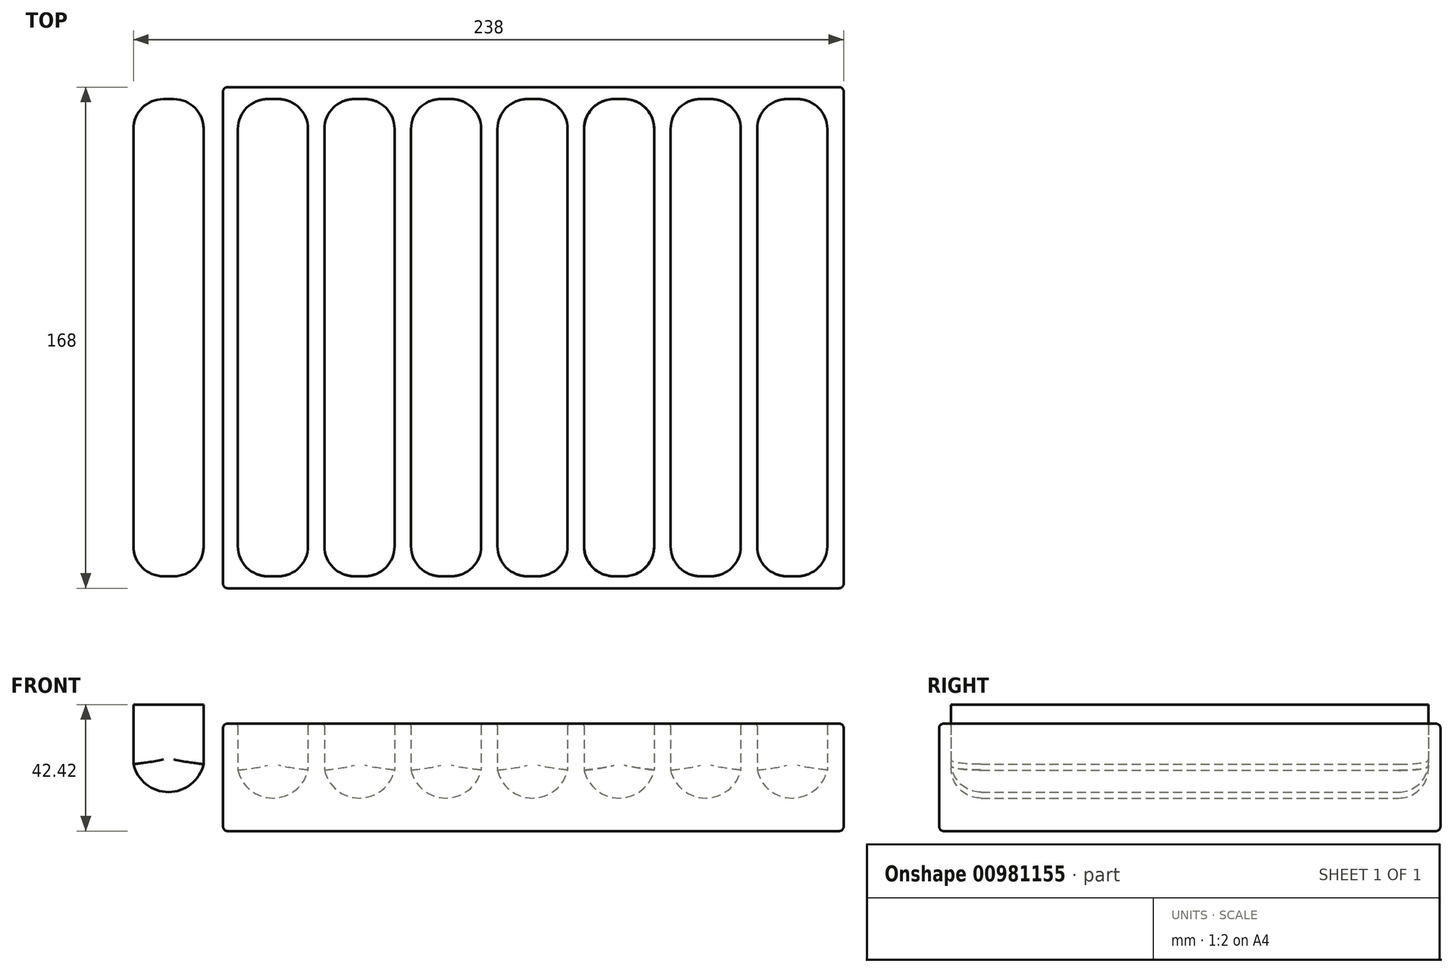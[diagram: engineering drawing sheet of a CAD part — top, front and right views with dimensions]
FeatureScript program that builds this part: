
annotation { "Feature Type Name" : "Feature", "Feature Type Description" : "" }
export const myFeature = defineFeature(function(context is Context, id is Id, definition is map)
    precondition{}
    {
        {
            var Q0;
            Q0=qCreatedBy(makeId("Top.planeOp"),FACE);
            var sketch = newSketch(context, id + "F0", { "sketchPlane" : qUnion([Q0])});
            skLineSegment(sketch, "E0.bottom", {"start": v(104, -84) * mm, "end": v(-104, -84) * mm});
            skLineSegment(sketch, "E0.top", {"start": v(104, 84) * mm, "end": v(-104, 84) * mm});
            skLineSegment(sketch, "E0.left", {"start": v(104, -84) * mm, "end": v(104, 84) * mm});
            skLineSegment(sketch, "E0.right", {"start": v(-104, -84) * mm, "end": v(-104, 84) * mm});
            skPoint(sketch, "E0.middle", {"position": v(0, 0) * mm});
            skSolve(sketch);
        }
        {
            var Q0;
            Q0=qSketchRegion(id+"F0",true);
            extrude(context, id + "F1", {"entities" : qUnion([Q0]), "depth" : 36 * mm, "offsetDistance" : 25 * mm});
        }
        {
            var Q0;
            Q0=qCreatedBy(makeId("Front.planeOp"),FACE);
            var sketch = newSketch(context, id + "F2", { "sketchPlane" : qUnion([Q0])});
            skLineSegment(sketch, "E1.bottom", {"start": v(-134, 42.42) * mm, "end": v(-110.5, 42.42) * mm});
            skLineSegment(sketch, "E1.top", {"start": v(-134, 22.42) * mm, "end": v(-110.5, 22.42) * mm});
            skLineSegment(sketch, "E1.left", {"start": v(-134, 42.42) * mm, "end": v(-134, 22.42) * mm});
            skLineSegment(sketch, "E1.right", {"start": v(-110.5, 42.42) * mm, "end": v(-110.5, 22.42) * mm});
            skArc(sketch, "E2", {"start": v(-134, 22.42) * mm, "mid": v(-122.25, 13.06) * mm, "end": v(-110.5, 22.42) * mm});
            skSolve(sketch);
        }
        {
            var Q0;
            Q0=makeQuery(id+"F2.imprint","IMPRINT",FACE,{"disambiguationData":[TD([[makeQuery(id+"F2.imprint","IMPRINT",EDGE,{"derivedFrom":sQuery(id+"F2.wireOp",EDGE,"E1.bottom")}),-1.0]])]});
            var Q1;
            Q1=makeQuery(id+"F2.imprint","IMPRINT",FACE,{"disambiguationData":[TD([[makeQuery(id+"F2.imprint","IMPRINT",EDGE,{"derivedFrom":sQuery(id+"F2.wireOp",EDGE,"E1.top")}),-1.0]])]});
            extrude(context, id + "F3", {"entities" : qUnion([Q0, Q1]), "depth" : 160 * mm, "offsetDistance" : 25 * mm, "symmetric" : true});
        }
        {
            var Q0;
            Q0=makeQuery(id+"F3.opExtrude","CAP_EDGE",EDGE,{"disambiguationData":[OSD([sQuery(id+"F2.wireOp",EDGE,"E1.left")])],"isStart":false});
            var Q1;
            Q1=makeQuery(id+"F3.opExtrude","CAP_EDGE",EDGE,{"disambiguationData":[OSD([sQuery(id+"F2.wireOp",EDGE,"E1.left")])],"isStart":true});
            var Q2;
            Q2=makeQuery(id+"F3.opExtrude","CAP_EDGE",EDGE,{"disambiguationData":[OSD([sQuery(id+"F2.wireOp",EDGE,"E1.right")])],"isStart":false});
            var Q3;
            Q3=makeQuery(id+"F3.opExtrude","CAP_EDGE",EDGE,{"disambiguationData":[OSD([sQuery(id+"F2.wireOp",EDGE,"E1.right")])],"isStart":true});
            var Q4;
            Q4=makeQuery(id+"F3.opExtrude","CAP_EDGE",EDGE,{"disambiguationData":[OSD([sQuery(id+"F2.wireOp",EDGE,"E2")])],"isStart":false});
            var Q5;
            Q5=makeQuery(id+"F3.opExtrude","CAP_EDGE",EDGE,{"disambiguationData":[OSD([sQuery(id+"F2.wireOp",EDGE,"E2")])],"isStart":true});
            fillet(context, id + "F4", {"entities" : qUnion([Q0, Q1, Q2, Q3, Q4, Q5]), "tangentPropagation" : true, "radius" : 10 * mm, "defaultsChanged" : true, "vertexSettings" : [], "allowEdgeOverflow" : false});
        }
        {
            var Q0;
            Q0=makeQuery(id+"F3.opExtrude","SWEPT_BODY",BODY,{"disambiguationData":[OSD([sQuery(id+"F2.wireOp",EDGE,"E1.bottom"),sQuery(id+"F2.wireOp",EDGE,"E1.left"),sQuery(id+"F2.wireOp",EDGE,"E1.right"),sQuery(id+"F2.wireOp",EDGE,"E2")])]});
            transform(context, id + "F5", {"entities" : qUnion([Q0]), "transformType" : TransformType.TRANSLATION_3D, "dx" : 35 * mm, "dy" : 0 * mm, "dz" : -2 * mm, "makeCopy" : true});
        }
        {
            var Q0;
            Q0=makeQuery(id+"F5.opPattern","COPY",BODY,{"derivedFrom":makeQuery(id+"F3.opExtrude","SWEPT_BODY",BODY,{"disambiguationData":[OSD([sQuery(id+"F2.wireOp",EDGE,"E1.bottom"),sQuery(id+"F2.wireOp",EDGE,"E1.left"),sQuery(id+"F2.wireOp",EDGE,"E1.right"),sQuery(id+"F2.wireOp",EDGE,"E2")])]}),"instanceName":"1"});
            transform(context, id + "F6", {"entities" : qUnion([Q0]), "transformType" : TransformType.TRANSLATION_3D, "dx" : 29 * mm, "dy" : 0 * mm, "dz" : 0 * mm, "makeCopy" : true});
        }
        {
            var Q0;
            Q0=makeQuery(id+"F6.opPattern","COPY",BODY,{"derivedFrom":makeQuery(id+"F5.opPattern","COPY",BODY,{"derivedFrom":makeQuery(id+"F3.opExtrude","SWEPT_BODY",BODY,{"disambiguationData":[OSD([sQuery(id+"F2.wireOp",EDGE,"E1.bottom"),sQuery(id+"F2.wireOp",EDGE,"E1.left"),sQuery(id+"F2.wireOp",EDGE,"E1.right"),sQuery(id+"F2.wireOp",EDGE,"E2")])]}),"instanceName":"1"}),"instanceName":"1"});
            transform(context, id + "F7", {"entities" : qUnion([Q0]), "transformType" : TransformType.TRANSLATION_3D, "dx" : 29 * mm, "dy" : 0 * mm, "dz" : 0 * mm, "makeCopy" : true});
        }
        {
            var Q0;
            Q0=makeQuery(id+"F7.opPattern","COPY",BODY,{"derivedFrom":makeQuery(id+"F6.opPattern","COPY",BODY,{"derivedFrom":makeQuery(id+"F5.opPattern","COPY",BODY,{"derivedFrom":makeQuery(id+"F3.opExtrude","SWEPT_BODY",BODY,{"disambiguationData":[OSD([sQuery(id+"F2.wireOp",EDGE,"E1.bottom"),sQuery(id+"F2.wireOp",EDGE,"E1.left"),sQuery(id+"F2.wireOp",EDGE,"E1.right"),sQuery(id+"F2.wireOp",EDGE,"E2")])]}),"instanceName":"1"}),"instanceName":"1"}),"instanceName":"1"});
            transform(context, id + "F8", {"entities" : qUnion([Q0]), "transformType" : TransformType.TRANSLATION_3D, "dx" : 29 * mm, "dy" : 0 * mm, "dz" : 0 * mm, "makeCopy" : true});
        }
        {
            var Q0;
            Q0=makeQuery(id+"F8.opPattern","COPY",BODY,{"derivedFrom":makeQuery(id+"F7.opPattern","COPY",BODY,{"derivedFrom":makeQuery(id+"F6.opPattern","COPY",BODY,{"derivedFrom":makeQuery(id+"F5.opPattern","COPY",BODY,{"derivedFrom":makeQuery(id+"F3.opExtrude","SWEPT_BODY",BODY,{"disambiguationData":[OSD([sQuery(id+"F2.wireOp",EDGE,"E1.bottom"),sQuery(id+"F2.wireOp",EDGE,"E1.left"),sQuery(id+"F2.wireOp",EDGE,"E1.right"),sQuery(id+"F2.wireOp",EDGE,"E2")])]}),"instanceName":"1"}),"instanceName":"1"}),"instanceName":"1"}),"instanceName":"1"});
            transform(context, id + "F9", {"entities" : qUnion([Q0]), "transformType" : TransformType.TRANSLATION_3D, "dx" : 29 * mm, "dy" : 0 * mm, "dz" : 0 * mm, "makeCopy" : true});
        }
        {
            var Q0;
            Q0=makeQuery(id+"F9.opPattern","COPY",BODY,{"derivedFrom":makeQuery(id+"F8.opPattern","COPY",BODY,{"derivedFrom":makeQuery(id+"F7.opPattern","COPY",BODY,{"derivedFrom":makeQuery(id+"F6.opPattern","COPY",BODY,{"derivedFrom":makeQuery(id+"F5.opPattern","COPY",BODY,{"derivedFrom":makeQuery(id+"F3.opExtrude","SWEPT_BODY",BODY,{"disambiguationData":[OSD([sQuery(id+"F2.wireOp",EDGE,"E1.bottom"),sQuery(id+"F2.wireOp",EDGE,"E1.left"),sQuery(id+"F2.wireOp",EDGE,"E1.right"),sQuery(id+"F2.wireOp",EDGE,"E2")])]}),"instanceName":"1"}),"instanceName":"1"}),"instanceName":"1"}),"instanceName":"1"}),"instanceName":"1"});
            transform(context, id + "F10", {"entities" : qUnion([Q0]), "transformType" : TransformType.TRANSLATION_3D, "dx" : 29 * mm, "dy" : 0 * mm, "dz" : 0 * mm, "makeCopy" : true});
        }
        {
            var Q0;
            Q0=makeQuery(id+"F10.opPattern","COPY",BODY,{"derivedFrom":makeQuery(id+"F9.opPattern","COPY",BODY,{"derivedFrom":makeQuery(id+"F8.opPattern","COPY",BODY,{"derivedFrom":makeQuery(id+"F7.opPattern","COPY",BODY,{"derivedFrom":makeQuery(id+"F6.opPattern","COPY",BODY,{"derivedFrom":makeQuery(id+"F5.opPattern","COPY",BODY,{"derivedFrom":makeQuery(id+"F3.opExtrude","SWEPT_BODY",BODY,{"disambiguationData":[OSD([sQuery(id+"F2.wireOp",EDGE,"E1.bottom"),sQuery(id+"F2.wireOp",EDGE,"E1.left"),sQuery(id+"F2.wireOp",EDGE,"E1.right"),sQuery(id+"F2.wireOp",EDGE,"E2")])]}),"instanceName":"1"}),"instanceName":"1"}),"instanceName":"1"}),"instanceName":"1"}),"instanceName":"1"}),"instanceName":"1"});
            transform(context, id + "F11", {"entities" : qUnion([Q0]), "transformType" : TransformType.TRANSLATION_3D, "dx" : 29 * mm, "dy" : 0 * mm, "dz" : 0 * mm, "makeCopy" : true});
        }
        {
            var Q0;
            Q0=makeQuery(id+"F5.opPattern","COPY",BODY,{"derivedFrom":makeQuery(id+"F3.opExtrude","SWEPT_BODY",BODY,{"disambiguationData":[OSD([sQuery(id+"F2.wireOp",EDGE,"E1.bottom"),sQuery(id+"F2.wireOp",EDGE,"E1.left"),sQuery(id+"F2.wireOp",EDGE,"E1.right"),sQuery(id+"F2.wireOp",EDGE,"E2")])]}),"instanceName":"1"});
            var Q1;
            Q1=makeQuery(id+"F6.opPattern","COPY",BODY,{"derivedFrom":makeQuery(id+"F5.opPattern","COPY",BODY,{"derivedFrom":makeQuery(id+"F3.opExtrude","SWEPT_BODY",BODY,{"disambiguationData":[OSD([sQuery(id+"F2.wireOp",EDGE,"E1.bottom"),sQuery(id+"F2.wireOp",EDGE,"E1.left"),sQuery(id+"F2.wireOp",EDGE,"E1.right"),sQuery(id+"F2.wireOp",EDGE,"E2")])]}),"instanceName":"1"}),"instanceName":"1"});
            var Q2;
            Q2=makeQuery(id+"F7.opPattern","COPY",BODY,{"derivedFrom":makeQuery(id+"F6.opPattern","COPY",BODY,{"derivedFrom":makeQuery(id+"F5.opPattern","COPY",BODY,{"derivedFrom":makeQuery(id+"F3.opExtrude","SWEPT_BODY",BODY,{"disambiguationData":[OSD([sQuery(id+"F2.wireOp",EDGE,"E1.bottom"),sQuery(id+"F2.wireOp",EDGE,"E1.left"),sQuery(id+"F2.wireOp",EDGE,"E1.right"),sQuery(id+"F2.wireOp",EDGE,"E2")])]}),"instanceName":"1"}),"instanceName":"1"}),"instanceName":"1"});
            var Q3;
            Q3=makeQuery(id+"F8.opPattern","COPY",BODY,{"derivedFrom":makeQuery(id+"F7.opPattern","COPY",BODY,{"derivedFrom":makeQuery(id+"F6.opPattern","COPY",BODY,{"derivedFrom":makeQuery(id+"F5.opPattern","COPY",BODY,{"derivedFrom":makeQuery(id+"F3.opExtrude","SWEPT_BODY",BODY,{"disambiguationData":[OSD([sQuery(id+"F2.wireOp",EDGE,"E1.bottom"),sQuery(id+"F2.wireOp",EDGE,"E1.left"),sQuery(id+"F2.wireOp",EDGE,"E1.right"),sQuery(id+"F2.wireOp",EDGE,"E2")])]}),"instanceName":"1"}),"instanceName":"1"}),"instanceName":"1"}),"instanceName":"1"});
            var Q4;
            Q4=makeQuery(id+"F10.opPattern","COPY",BODY,{"derivedFrom":makeQuery(id+"F9.opPattern","COPY",BODY,{"derivedFrom":makeQuery(id+"F8.opPattern","COPY",BODY,{"derivedFrom":makeQuery(id+"F7.opPattern","COPY",BODY,{"derivedFrom":makeQuery(id+"F6.opPattern","COPY",BODY,{"derivedFrom":makeQuery(id+"F5.opPattern","COPY",BODY,{"derivedFrom":makeQuery(id+"F3.opExtrude","SWEPT_BODY",BODY,{"disambiguationData":[OSD([sQuery(id+"F2.wireOp",EDGE,"E1.bottom"),sQuery(id+"F2.wireOp",EDGE,"E1.left"),sQuery(id+"F2.wireOp",EDGE,"E1.right"),sQuery(id+"F2.wireOp",EDGE,"E2")])]}),"instanceName":"1"}),"instanceName":"1"}),"instanceName":"1"}),"instanceName":"1"}),"instanceName":"1"}),"instanceName":"1"});
            var Q5;
            Q5=makeQuery(id+"F9.opPattern","COPY",BODY,{"derivedFrom":makeQuery(id+"F8.opPattern","COPY",BODY,{"derivedFrom":makeQuery(id+"F7.opPattern","COPY",BODY,{"derivedFrom":makeQuery(id+"F6.opPattern","COPY",BODY,{"derivedFrom":makeQuery(id+"F5.opPattern","COPY",BODY,{"derivedFrom":makeQuery(id+"F3.opExtrude","SWEPT_BODY",BODY,{"disambiguationData":[OSD([sQuery(id+"F2.wireOp",EDGE,"E1.bottom"),sQuery(id+"F2.wireOp",EDGE,"E1.left"),sQuery(id+"F2.wireOp",EDGE,"E1.right"),sQuery(id+"F2.wireOp",EDGE,"E2")])]}),"instanceName":"1"}),"instanceName":"1"}),"instanceName":"1"}),"instanceName":"1"}),"instanceName":"1"});
            var Q6;
            Q6=makeQuery(id+"F11.opPattern","COPY",BODY,{"derivedFrom":makeQuery(id+"F10.opPattern","COPY",BODY,{"derivedFrom":makeQuery(id+"F9.opPattern","COPY",BODY,{"derivedFrom":makeQuery(id+"F8.opPattern","COPY",BODY,{"derivedFrom":makeQuery(id+"F7.opPattern","COPY",BODY,{"derivedFrom":makeQuery(id+"F6.opPattern","COPY",BODY,{"derivedFrom":makeQuery(id+"F5.opPattern","COPY",BODY,{"derivedFrom":makeQuery(id+"F3.opExtrude","SWEPT_BODY",BODY,{"disambiguationData":[OSD([sQuery(id+"F2.wireOp",EDGE,"E1.bottom"),sQuery(id+"F2.wireOp",EDGE,"E1.left"),sQuery(id+"F2.wireOp",EDGE,"E1.right"),sQuery(id+"F2.wireOp",EDGE,"E2")])]}),"instanceName":"1"}),"instanceName":"1"}),"instanceName":"1"}),"instanceName":"1"}),"instanceName":"1"}),"instanceName":"1"}),"instanceName":"1"});
            var Q7;
            Q7=makeQuery(id+"F1.opExtrude","SWEPT_BODY",BODY,{"disambiguationData":[OSD([sQuery(id+"F0.wireOp",EDGE,"E0.bottom"),sQuery(id+"F0.wireOp",EDGE,"E0.top"),sQuery(id+"F0.wireOp",EDGE,"E0.left"),sQuery(id+"F0.wireOp",EDGE,"E0.right")])]});
            booleanBodies(context, id + "F12", {"operationType" : BooleanOperationType.SUBTRACTION, "tools" : qUnion([Q0, Q1, Q2, Q3, Q4, Q5, Q6]), "targets" : qUnion([Q7])});
        }
        {
            var Q0;
            Q0=makeQuery(id+"F1.opExtrude","CAP_EDGE",EDGE,{"disambiguationData":[OSD([sQuery(id+"F0.wireOp",EDGE,"E0.right")])],"isStart":false});
            var Q1;
            Q1=makeQuery(id+"F1.opExtrude","CAP_EDGE",EDGE,{"disambiguationData":[OSD([sQuery(id+"F0.wireOp",EDGE,"E0.top")])],"isStart":false});
            var Q2;
            Q2=makeQuery(id+"F1.opExtrude","CAP_EDGE",EDGE,{"disambiguationData":[OSD([sQuery(id+"F0.wireOp",EDGE,"E0.left")])],"isStart":false});
            var Q3;
            Q3=makeQuery(id+"F1.opExtrude","CAP_EDGE",EDGE,{"disambiguationData":[OSD([sQuery(id+"F0.wireOp",EDGE,"E0.left")])],"isStart":true});
            var Q4;
            Q4=makeQuery(id+"F1.opExtrude","SWEPT_EDGE",EDGE,{"disambiguationData":[OSD([sQuery(id+"F0.wireOp",EDGE,"E0.top"),sQuery(id+"F0.wireOp",EDGE,"E0.left")])]});
            var Q5;
            Q5=makeQuery(id+"F1.opExtrude","CAP_EDGE",EDGE,{"disambiguationData":[OSD([sQuery(id+"F0.wireOp",EDGE,"E0.top")])],"isStart":true});
            var Q6;
            Q6=makeQuery(id+"F1.opExtrude","SWEPT_EDGE",EDGE,{"disambiguationData":[OSD([sQuery(id+"F0.wireOp",EDGE,"E0.top"),sQuery(id+"F0.wireOp",EDGE,"E0.right")])]});
            var Q7;
            Q7=makeQuery(id+"F1.opExtrude","CAP_EDGE",EDGE,{"disambiguationData":[OSD([sQuery(id+"F0.wireOp",EDGE,"E0.right")])],"isStart":true});
            var Q8;
            Q8=makeQuery(id+"F1.opExtrude","CAP_EDGE",EDGE,{"disambiguationData":[OSD([sQuery(id+"F0.wireOp",EDGE,"E0.bottom")])],"isStart":false});
            var Q9;
            Q9=makeQuery(id+"F1.opExtrude","CAP_EDGE",EDGE,{"disambiguationData":[OSD([sQuery(id+"F0.wireOp",EDGE,"E0.bottom")])],"isStart":true});
            var Q10;
            Q10=makeQuery(id+"F1.opExtrude","SWEPT_EDGE",EDGE,{"disambiguationData":[OSD([sQuery(id+"F0.wireOp",EDGE,"E0.bottom"),sQuery(id+"F0.wireOp",EDGE,"E0.right")])]});
            var Q11;
            Q11=makeQuery(id+"F1.opExtrude","SWEPT_EDGE",EDGE,{"disambiguationData":[OSD([sQuery(id+"F0.wireOp",EDGE,"E0.bottom"),sQuery(id+"F0.wireOp",EDGE,"E0.left")])]});
            fillet(context, id + "F13", {"entities" : qUnion([Q0, Q1, Q2, Q3, Q4, Q5, Q6, Q7, Q8, Q9, Q10, Q11]), "tangentPropagation" : true, "radius" : 1.5 * mm, "defaultsChanged" : true, "vertexSettings" : [], "allowEdgeOverflow" : false});
        }
        {
            var Q0;
            Q0=makeQuery(id+"F12.opBoolean","INTERSECT",EDGE,{"derivedFrom":[makeQuery(id+"F1.opExtrude","CAP_FACE",FACE,{"disambiguationData":[OSD([sQuery(id+"F0.wireOp",EDGE,"E0.bottom"),sQuery(id+"F0.wireOp",EDGE,"E0.top"),sQuery(id+"F0.wireOp",EDGE,"E0.left"),sQuery(id+"F0.wireOp",EDGE,"E0.right")])],"isStart":false}),makeQuery(id+"F5.opPattern","COPY",FACE,{"derivedFrom":makeQuery(id+"F3.opExtrude","SWEPT_FACE",FACE,{"disambiguationData":[OSD([sQuery(id+"F2.wireOp",EDGE,"E1.left")])]}),"instanceName":"1"})]});
            var Q1;
            Q1=makeQuery(id+"F12.opBoolean","INTERSECT",EDGE,{"derivedFrom":[makeQuery(id+"F1.opExtrude","CAP_FACE",FACE,{"disambiguationData":[OSD([sQuery(id+"F0.wireOp",EDGE,"E0.bottom"),sQuery(id+"F0.wireOp",EDGE,"E0.top"),sQuery(id+"F0.wireOp",EDGE,"E0.left"),sQuery(id+"F0.wireOp",EDGE,"E0.right")])],"isStart":false}),makeQuery(id+"F6.opPattern","COPY",FACE,{"derivedFrom":makeQuery(id+"F5.opPattern","COPY",FACE,{"derivedFrom":makeQuery(id+"F3.opExtrude","SWEPT_FACE",FACE,{"disambiguationData":[OSD([sQuery(id+"F2.wireOp",EDGE,"E1.left")])]}),"instanceName":"1"}),"instanceName":"1"})]});
            var Q2;
            Q2=makeQuery(id+"F12.opBoolean","INTERSECT",EDGE,{"derivedFrom":[makeQuery(id+"F1.opExtrude","CAP_FACE",FACE,{"disambiguationData":[OSD([sQuery(id+"F0.wireOp",EDGE,"E0.bottom"),sQuery(id+"F0.wireOp",EDGE,"E0.top"),sQuery(id+"F0.wireOp",EDGE,"E0.left"),sQuery(id+"F0.wireOp",EDGE,"E0.right")])],"isStart":false}),makeQuery(id+"F7.opPattern","COPY",FACE,{"derivedFrom":makeQuery(id+"F6.opPattern","COPY",FACE,{"derivedFrom":makeQuery(id+"F5.opPattern","COPY",FACE,{"derivedFrom":makeQuery(id+"F3.opExtrude","SWEPT_FACE",FACE,{"disambiguationData":[OSD([sQuery(id+"F2.wireOp",EDGE,"E1.left")])]}),"instanceName":"1"}),"instanceName":"1"}),"instanceName":"1"})]});
            var Q3;
            Q3=makeQuery(id+"F12.opBoolean","INTERSECT",EDGE,{"derivedFrom":[makeQuery(id+"F1.opExtrude","CAP_FACE",FACE,{"disambiguationData":[OSD([sQuery(id+"F0.wireOp",EDGE,"E0.bottom"),sQuery(id+"F0.wireOp",EDGE,"E0.top"),sQuery(id+"F0.wireOp",EDGE,"E0.left"),sQuery(id+"F0.wireOp",EDGE,"E0.right")])],"isStart":false}),makeQuery(id+"F8.opPattern","COPY",FACE,{"derivedFrom":makeQuery(id+"F7.opPattern","COPY",FACE,{"derivedFrom":makeQuery(id+"F6.opPattern","COPY",FACE,{"derivedFrom":makeQuery(id+"F5.opPattern","COPY",FACE,{"derivedFrom":makeQuery(id+"F3.opExtrude","SWEPT_FACE",FACE,{"disambiguationData":[OSD([sQuery(id+"F2.wireOp",EDGE,"E1.left")])]}),"instanceName":"1"}),"instanceName":"1"}),"instanceName":"1"}),"instanceName":"1"})]});
            var Q4;
            Q4=makeQuery(id+"F12.opBoolean","COPY",FACE,{"derivedFrom":makeQuery(id+"F9.opPattern","COPY",FACE,{"derivedFrom":makeQuery(id+"F8.opPattern","COPY",FACE,{"derivedFrom":makeQuery(id+"F7.opPattern","COPY",FACE,{"derivedFrom":makeQuery(id+"F6.opPattern","COPY",FACE,{"derivedFrom":makeQuery(id+"F5.opPattern","COPY",FACE,{"derivedFrom":makeQuery(id+"F3.opExtrude","SWEPT_FACE",FACE,{"disambiguationData":[OSD([sQuery(id+"F2.wireOp",EDGE,"E2")])]}),"instanceName":"1"}),"instanceName":"1"}),"instanceName":"1"}),"instanceName":"1"}),"instanceName":"1"})});
            var Q5;
            Q5=makeQuery(id+"F12.opBoolean","INTERSECT",EDGE,{"derivedFrom":[makeQuery(id+"F1.opExtrude","CAP_FACE",FACE,{"disambiguationData":[OSD([sQuery(id+"F0.wireOp",EDGE,"E0.bottom"),sQuery(id+"F0.wireOp",EDGE,"E0.top"),sQuery(id+"F0.wireOp",EDGE,"E0.left"),sQuery(id+"F0.wireOp",EDGE,"E0.right")])],"isStart":false}),makeQuery(id+"F9.opPattern","COPY",FACE,{"derivedFrom":makeQuery(id+"F8.opPattern","COPY",FACE,{"derivedFrom":makeQuery(id+"F7.opPattern","COPY",FACE,{"derivedFrom":makeQuery(id+"F6.opPattern","COPY",FACE,{"derivedFrom":makeQuery(id+"F5.opPattern","COPY",FACE,{"derivedFrom":makeQuery(id+"F3.opExtrude","SWEPT_FACE",FACE,{"disambiguationData":[OSD([sQuery(id+"F2.wireOp",EDGE,"E1.left")])]}),"instanceName":"1"}),"instanceName":"1"}),"instanceName":"1"}),"instanceName":"1"}),"instanceName":"1"})]});
            var Q6;
            Q6=makeQuery(id+"F12.opBoolean","INTERSECT",EDGE,{"derivedFrom":[makeQuery(id+"F1.opExtrude","CAP_FACE",FACE,{"disambiguationData":[OSD([sQuery(id+"F0.wireOp",EDGE,"E0.bottom"),sQuery(id+"F0.wireOp",EDGE,"E0.top"),sQuery(id+"F0.wireOp",EDGE,"E0.left"),sQuery(id+"F0.wireOp",EDGE,"E0.right")])],"isStart":false}),makeQuery(id+"F10.opPattern","COPY",FACE,{"derivedFrom":makeQuery(id+"F9.opPattern","COPY",FACE,{"derivedFrom":makeQuery(id+"F8.opPattern","COPY",FACE,{"derivedFrom":makeQuery(id+"F7.opPattern","COPY",FACE,{"derivedFrom":makeQuery(id+"F6.opPattern","COPY",FACE,{"derivedFrom":makeQuery(id+"F5.opPattern","COPY",FACE,{"derivedFrom":makeQuery(id+"F3.opExtrude","SWEPT_FACE",FACE,{"disambiguationData":[OSD([sQuery(id+"F2.wireOp",EDGE,"E1.left")])]}),"instanceName":"1"}),"instanceName":"1"}),"instanceName":"1"}),"instanceName":"1"}),"instanceName":"1"}),"instanceName":"1"})]});
            var Q7;
            Q7=makeQuery(id+"F12.opBoolean","INTERSECT",EDGE,{"derivedFrom":[makeQuery(id+"F1.opExtrude","CAP_FACE",FACE,{"disambiguationData":[OSD([sQuery(id+"F0.wireOp",EDGE,"E0.bottom"),sQuery(id+"F0.wireOp",EDGE,"E0.top"),sQuery(id+"F0.wireOp",EDGE,"E0.left"),sQuery(id+"F0.wireOp",EDGE,"E0.right")])],"isStart":false}),makeQuery(id+"F11.opPattern","COPY",FACE,{"derivedFrom":makeQuery(id+"F10.opPattern","COPY",FACE,{"derivedFrom":makeQuery(id+"F9.opPattern","COPY",FACE,{"derivedFrom":makeQuery(id+"F8.opPattern","COPY",FACE,{"derivedFrom":makeQuery(id+"F7.opPattern","COPY",FACE,{"derivedFrom":makeQuery(id+"F6.opPattern","COPY",FACE,{"derivedFrom":makeQuery(id+"F5.opPattern","COPY",FACE,{"derivedFrom":makeQuery(id+"F3.opExtrude","SWEPT_FACE",FACE,{"disambiguationData":[OSD([sQuery(id+"F2.wireOp",EDGE,"E1.left")])]}),"instanceName":"1"}),"instanceName":"1"}),"instanceName":"1"}),"instanceName":"1"}),"instanceName":"1"}),"instanceName":"1"}),"instanceName":"1"})]});
            fillet(context, id + "F14", {"entities" : qUnion([Q0, Q1, Q2, Q3, Q4, Q5, Q6, Q7]), "tangentPropagation" : true, "radius" : .8 * mm, "defaultsChanged" : true, "vertexSettings" : [], "allowEdgeOverflow" : false});
        }
    });
